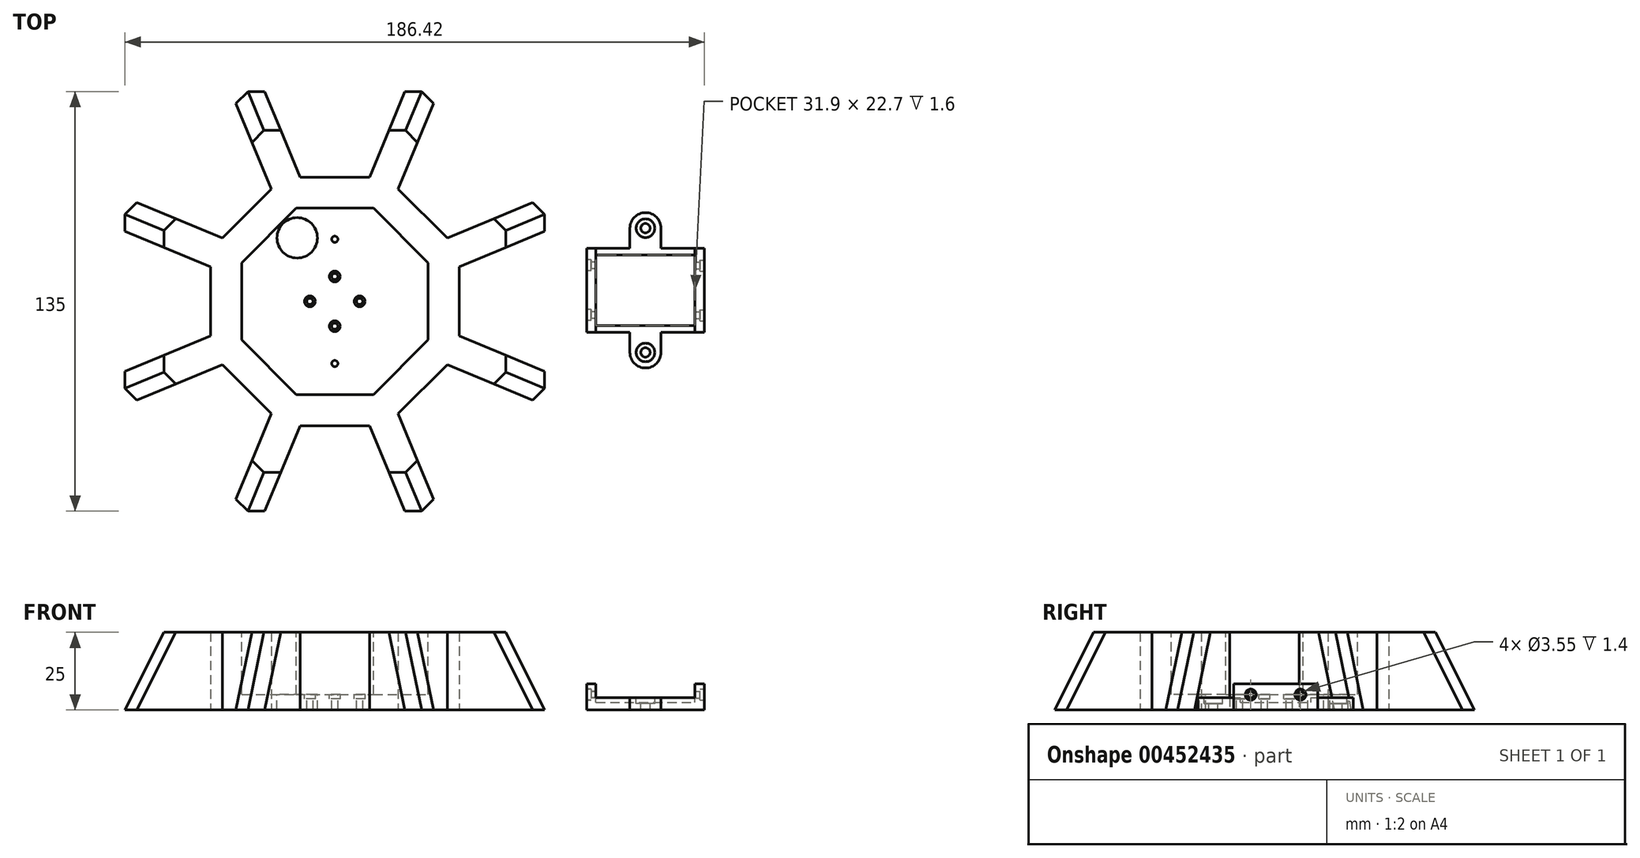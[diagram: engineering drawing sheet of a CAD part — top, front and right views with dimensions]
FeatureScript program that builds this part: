
annotation { "Feature Type Name" : "Feature", "Feature Type Description" : "" }
export const myFeature = defineFeature(function(context is Context, id is Id, definition is map)
    precondition{}
    {
        {
            var Q0;
            Q0=qCreatedBy(makeId("Top.planeOp"),FACE);
            cPlane(context, id + "F0", {"entities" : qUnion([Q0]), "cplaneType" : CPlaneType.OFFSET, "offset" : 0 * mm, "width" : 150 * mm, "height" : 150 * mm});
        }
        {
            var Q0;
            Q0=qCreatedBy(id+"F0.planeOp",FACE);
            var sketch = newSketch(context, id + "F1", { "sketchPlane" : qUnion([Q0])});
            skCircle(sketch, "E0.cCircle", {"center": v(0, 0) * mm, "radius": 75 * mm, "construction": true});
            skLineSegment(sketch, "E0.0", {"start": v(75, 31.07) * mm, "end": v(75, -31.07) * mm});
            skLineSegment(sketch, "E0.1", {"start": v(75, -31.07) * mm, "end": v(31.07, -75) * mm});
            skLineSegment(sketch, "E0.2", {"start": v(31.07, -75) * mm, "end": v(-31.07, -75) * mm});
            skLineSegment(sketch, "E0.3", {"start": v(-31.07, -75) * mm, "end": v(-75, -31.07) * mm});
            skLineSegment(sketch, "E0.4", {"start": v(-75, -31.07) * mm, "end": v(-75, 31.07) * mm});
            skLineSegment(sketch, "E0.5", {"start": v(-75, 31.07) * mm, "end": v(-31.07, 75) * mm});
            skLineSegment(sketch, "E0.6", {"start": v(-31.07, 75) * mm, "end": v(31.07, 75) * mm});
            skLineSegment(sketch, "E0.7", {"start": v(31.07, 75) * mm, "end": v(75, 31.07) * mm});
            skSolve(sketch);
        }
        {
            var Q0;
            Q0=qSketchRegion(id+"F1",true);
            extrude(context, id + "F2", {"entities" : qUnion([Q0]), "depth" : 25 * mm});
        }
        {
            var Q0;
            Q0=makeQuery(id+"F2.opExtrude","CAP_EDGE",EDGE,{"disambiguationData":[OSD([sQuery(id+"F1.wireOp",EDGE,"E0.4")])],"isStart":false});
            var Q1;
            Q1=makeQuery(id+"F2.opExtrude","CAP_EDGE",EDGE,{"disambiguationData":[OSD([sQuery(id+"F1.wireOp",EDGE,"E0.0")])],"isStart":false});
            var Q2;
            Q2=makeQuery(id+"F2.opExtrude","CAP_EDGE",EDGE,{"disambiguationData":[OSD([sQuery(id+"F1.wireOp",EDGE,"E0.7")])],"isStart":false});
            var Q3;
            Q3=makeQuery(id+"F2.opExtrude","CAP_EDGE",EDGE,{"disambiguationData":[OSD([sQuery(id+"F1.wireOp",EDGE,"E0.6")])],"isStart":false});
            var Q4;
            Q4=makeQuery(id+"F2.opExtrude","CAP_EDGE",EDGE,{"disambiguationData":[OSD([sQuery(id+"F1.wireOp",EDGE,"E0.5")])],"isStart":false});
            var Q5;
            Q5=makeQuery(id+"F2.opExtrude","CAP_EDGE",EDGE,{"disambiguationData":[OSD([sQuery(id+"F1.wireOp",EDGE,"E0.3")])],"isStart":false});
            var Q6;
            Q6=makeQuery(id+"F2.opExtrude","CAP_EDGE",EDGE,{"disambiguationData":[OSD([sQuery(id+"F1.wireOp",EDGE,"E0.2")])],"isStart":false});
            var Q7;
            Q7=makeQuery(id+"F2.opExtrude","CAP_EDGE",EDGE,{"disambiguationData":[OSD([sQuery(id+"F1.wireOp",EDGE,"E0.1")])],"isStart":false});
            chamfer(context, id + "F3", {"entities" : qUnion([Q0, Q1, Q2, Q3, Q4, Q5, Q6, Q7]), "chamferType" : ChamferType.TWO_OFFSETS, "width1" : 20 * mm, "oppositeDirection" : false, "width2" : 40 * mm, "tangentPropagation" : true});
        }
        {
            var Q0;
            Q0=makeQuery(id+"F2.opExtrude","CAP_FACE",FACE,{"disambiguationData":[OSD([sQuery(id+"F1.wireOp",EDGE,"E0.0"),sQuery(id+"F1.wireOp",EDGE,"E0.1"),sQuery(id+"F1.wireOp",EDGE,"E0.2"),sQuery(id+"F1.wireOp",EDGE,"E0.3"),sQuery(id+"F1.wireOp",EDGE,"E0.4"),sQuery(id+"F1.wireOp",EDGE,"E0.5"),sQuery(id+"F1.wireOp",EDGE,"E0.6"),sQuery(id+"F1.wireOp",EDGE,"E0.7")])],"isStart":false});
            var sketch = newSketch(context, id + "F4", { "sketchPlane" : qUnion([Q0])});
            skPoint(sketch, "E1.middle", {"position": v(0, 0) * mm});
            skLineSegment(sketch, "E2.0", {"start": v(-14.5, 35) * mm, "end": v(-35, 14.5) * mm});
            skLineSegment(sketch, "E2.1", {"start": v(14.5, 35) * mm, "end": v(-14.5, 35) * mm});
            skLineSegment(sketch, "E2.2", {"start": v(35, 14.5) * mm, "end": v(14.5, 35) * mm});
            skLineSegment(sketch, "E2.3", {"start": v(35, -14.5) * mm, "end": v(35, 14.5) * mm});
            skLineSegment(sketch, "E2.4", {"start": v(14.5, -35) * mm, "end": v(35, -14.5) * mm});
            skLineSegment(sketch, "E2.5", {"start": v(-14.5, -35) * mm, "end": v(14.5, -35) * mm});
            skLineSegment(sketch, "E2.6", {"start": v(-35, -14.5) * mm, "end": v(-14.5, -35) * mm});
            skLineSegment(sketch, "E2.7", {"start": v(-35, 14.5) * mm, "end": v(-35, -14.5) * mm});
            skLineSegment(sketch, "E3.0", {"start": v(-12.43, -30) * mm, "end": v(12.43, -30) * mm});
            skLineSegment(sketch, "E3.1", {"start": v(-30, -12.43) * mm, "end": v(-12.43, -30) * mm});
            skLineSegment(sketch, "E3.2", {"start": v(12.43, -30) * mm, "end": v(30, -12.43) * mm});
            skLineSegment(sketch, "E3.3", {"start": v(-30, 12.43) * mm, "end": v(-30, -12.43) * mm});
            skLineSegment(sketch, "E3.4", {"start": v(30, -12.43) * mm, "end": v(30, 12.43) * mm});
            skLineSegment(sketch, "E3.5", {"start": v(30, 12.43) * mm, "end": v(12.43, 30) * mm});
            skLineSegment(sketch, "E3.6", {"start": v(12.43, 30) * mm, "end": v(-12.43, 30) * mm});
            skLineSegment(sketch, "E3.7", {"start": v(-12.43, 30) * mm, "end": v(-30, 12.43) * mm});
            skSolve(sketch);
        }
        {
            var Q0;
            Q0=makeQuery(id+"F4.imprint","IMPRINT",FACE,{"disambiguationData":[TD([[makeQuery(id+"F4.imprint","IMPRINT",EDGE,{"derivedFrom":sQuery(id+"F4.wireOp",EDGE,"E1.bottom")}),-1.0]])]});
            var Q1;
            Q1=makeQuery(id+"F4.imprint","IMPRINT",FACE,{"disambiguationData":[TD([[makeQuery(id+"F4.imprint","IMPRINT",EDGE,{"derivedFrom":sQuery(id+"F4.wireOp",EDGE,"E3.0")}),1.0]])]});
            extrude(context, id + "F5", {"entities" : qUnion([Q0, Q1]), "operationType" : NewBodyOperationType.REMOVE, "oppositeDirection" : true, "depth" : 20 * mm, "offsetDistance" : 25 * mm});
        }
        {
            var Q0;
            Q0=makeQuery(id+"F5.boolean.opBoolean","COPY",FACE,{"derivedFrom":makeQuery(id+"F5.opExtrude","CAP_FACE",FACE,{"disambiguationData":[OSD([sQuery(id+"F4.wireOp",EDGE,"E3.0"),sQuery(id+"F4.wireOp",EDGE,"E3.1"),sQuery(id+"F4.wireOp",EDGE,"E3.2"),sQuery(id+"F4.wireOp",EDGE,"E3.3"),sQuery(id+"F4.wireOp",EDGE,"E3.4"),sQuery(id+"F4.wireOp",EDGE,"E3.5"),sQuery(id+"F4.wireOp",EDGE,"E3.6"),sQuery(id+"F4.wireOp",EDGE,"E3.7")])],"isStart":false})});
            var sketch = newSketch(context, id + "F6", { "sketchPlane" : qUnion([Q0])});
            skCircle(sketch, "E4", {"center": v(0, 0) * mm, "radius": 8 * mm, "construction": true});
            skCircle(sketch, "E5", {"center": v(0, 8) * mm, "radius": 1 * mm});
            skCircle(sketch, "E6", {"center": v(8, 0) * mm, "radius": 1 * mm});
            skCircle(sketch, "E7", {"center": v(0, -8) * mm, "radius": 1 * mm});
            skCircle(sketch, "E8", {"center": v(-8, 0) * mm, "radius": 1 * mm});
            skCircle(sketch, "E9", {"center": v(0, 0) * mm, "radius": 12 * mm});
            skCircle(sketch, "E10", {"center": v(0, 8) * mm, "radius": 1.75 * mm});
            skCircle(sketch, "E11", {"center": v(8, 0) * mm, "radius": 1.75 * mm});
            skCircle(sketch, "E12", {"center": v(0, -8) * mm, "radius": 1.75 * mm});
            skCircle(sketch, "E13", {"center": v(-8, 0) * mm, "radius": 1.75 * mm});
            skSolve(sketch);
        }
        {
            var Q0;
            Q0=makeQuery(id+"F6.imprint","IMPRINT",FACE,{"disambiguationData":[TD([[makeQuery(id+"F6.imprint","IMPRINT",EDGE,{"derivedFrom":sQuery(id+"F6.wireOp",EDGE,"E6")}),1.0]])]});
            var Q1;
            Q1=makeQuery(id+"F6.imprint","IMPRINT",FACE,{"disambiguationData":[TD([[makeQuery(id+"F6.imprint","IMPRINT",EDGE,{"derivedFrom":sQuery(id+"F6.wireOp",EDGE,"E5")}),1.0]])]});
            var Q2;
            Q2=makeQuery(id+"F6.imprint","IMPRINT",FACE,{"disambiguationData":[TD([[makeQuery(id+"F6.imprint","IMPRINT",EDGE,{"derivedFrom":sQuery(id+"F6.wireOp",EDGE,"E8")}),1.0]])]});
            var Q3;
            Q3=makeQuery(id+"F6.imprint","IMPRINT",FACE,{"disambiguationData":[TD([[makeQuery(id+"F6.imprint","IMPRINT",EDGE,{"derivedFrom":sQuery(id+"F6.wireOp",EDGE,"E7")}),1.0]])]});
            extrude(context, id + "F7", {"entities" : qUnion([Q0, Q1, Q2, Q3]), "operationType" : NewBodyOperationType.REMOVE, "oppositeDirection" : true, "depth" : 25 * mm, "offsetDistance" : 25 * mm});
        }
        {
            var Q0;
            Q0=makeQuery(id+"F2.opExtrude","CAP_FACE",FACE,{"disambiguationData":[OSD([sQuery(id+"F1.wireOp",EDGE,"E0.0"),sQuery(id+"F1.wireOp",EDGE,"E0.1"),sQuery(id+"F1.wireOp",EDGE,"E0.2"),sQuery(id+"F1.wireOp",EDGE,"E0.3"),sQuery(id+"F1.wireOp",EDGE,"E0.4"),sQuery(id+"F1.wireOp",EDGE,"E0.5"),sQuery(id+"F1.wireOp",EDGE,"E0.6"),sQuery(id+"F1.wireOp",EDGE,"E0.7")])],"isStart":true});
            var sketch = newSketch(context, id + "F8", { "sketchPlane" : qUnion([Q0])});
            skLineSegment(sketch, "E14.0", {"start": v(35, -14.5) * mm, "end": v(14.5, -35) * mm});
            skLineSegment(sketch, "E14.1", {"start": v(31.07, -75) * mm, "end": v(14.5, -35) * mm});
            skLineSegment(sketch, "E14.2", {"start": v(31.07, -75) * mm, "end": v(75, -31.07) * mm});
            skLineSegment(sketch, "E14.3", {"start": v(75, -31.07) * mm, "end": v(35, -14.5) * mm});
            skLineSegment(sketch, "E14.4", {"start": v(75, -31.07) * mm, "end": v(75, 31.07) * mm});
            skLineSegment(sketch, "E14.5", {"start": v(75, 31.07) * mm, "end": v(31.07, 75) * mm});
            skLineSegment(sketch, "E14.6", {"start": v(31.07, 75) * mm, "end": v(-31.07, 75) * mm});
            skLineSegment(sketch, "E14.7", {"start": v(-31.07, 75) * mm, "end": v(-75, 31.07) * mm});
            skLineSegment(sketch, "E14.8", {"start": v(-75, 31.07) * mm, "end": v(-75, -31.07) * mm});
            skLineSegment(sketch, "E14.9", {"start": v(-75, -31.07) * mm, "end": v(-31.07, -75) * mm});
            skLineSegment(sketch, "E14.10", {"start": v(-31.07, -75) * mm, "end": v(31.07, -75) * mm});
            skLineSegment(sketch, "E14.11", {"start": v(-31.07, -75) * mm, "end": v(-14.5, -35) * mm});
            skLineSegment(sketch, "E14.12", {"start": v(-35, -14.5) * mm, "end": v(-75, -31.07) * mm});
            skLineSegment(sketch, "E14.13", {"start": v(-35, 14.5) * mm, "end": v(-75, 31.07) * mm});
            skLineSegment(sketch, "E14.14", {"start": v(-14.5, 35) * mm, "end": v(-31.07, 75) * mm});
            skLineSegment(sketch, "E14.15", {"start": v(14.5, 35) * mm, "end": v(31.07, 75) * mm});
            skLineSegment(sketch, "E14.16", {"start": v(75, 31.07) * mm, "end": v(35, 14.5) * mm});
            skLineSegment(sketch, "E14.17", {"start": v(35, 14.5) * mm, "end": v(35, -14.5) * mm});
            skLineSegment(sketch, "E14.18", {"start": v(14.5, 35) * mm, "end": v(35, 14.5) * mm});
            skLineSegment(sketch, "E14.19", {"start": v(-14.5, 35) * mm, "end": v(14.5, 35) * mm});
            skLineSegment(sketch, "E14.20", {"start": v(-35, 14.5) * mm, "end": v(-14.5, 35) * mm});
            skLineSegment(sketch, "E14.21", {"start": v(-35, -14.5) * mm, "end": v(-35, 14.5) * mm});
            skLineSegment(sketch, "E14.22", {"start": v(-14.5, -35) * mm, "end": v(-35, -14.5) * mm});
            skLineSegment(sketch, "E14.23", {"start": v(14.5, -35) * mm, "end": v(-14.5, -35) * mm});
            skLineSegment(sketch, "E15.0", {"start": v(11.16, 40) * mm, "end": v(23.58, 70) * mm});
            skLineSegment(sketch, "E15.1", {"start": v(-11.16, 40) * mm, "end": v(11.16, 40) * mm});
            skLineSegment(sketch, "E15.2", {"start": v(-11.16, 40) * mm, "end": v(-23.58, 70) * mm});
            skLineSegment(sketch, "E15.3", {"start": v(23.58, 70) * mm, "end": v(-23.58, 70) * mm});
            skLineSegment(sketch, "E16.0", {"start": v(20.4, 36.17) * mm, "end": v(32.82, 66.17) * mm});
            skLineSegment(sketch, "E16.1", {"start": v(20.4, 36.17) * mm, "end": v(36.17, 20.4) * mm});
            skLineSegment(sketch, "E16.2", {"start": v(66.17, 32.82) * mm, "end": v(36.17, 20.4) * mm});
            skLineSegment(sketch, "E16.3", {"start": v(66.17, 32.82) * mm, "end": v(32.82, 66.17) * mm});
            skLineSegment(sketch, "E17.0", {"start": v(70, 23.58) * mm, "end": v(40, 11.16) * mm});
            skLineSegment(sketch, "E17.1", {"start": v(70, -23.58) * mm, "end": v(70, 23.58) * mm});
            skLineSegment(sketch, "E17.2", {"start": v(70, -23.58) * mm, "end": v(40, -11.16) * mm});
            skLineSegment(sketch, "E17.3", {"start": v(40, 11.16) * mm, "end": v(40, -11.16) * mm});
            skLineSegment(sketch, "E18.0", {"start": v(66.17, -32.82) * mm, "end": v(36.17, -20.4) * mm});
            skLineSegment(sketch, "E18.1", {"start": v(32.82, -66.17) * mm, "end": v(66.17, -32.82) * mm});
            skLineSegment(sketch, "E18.2", {"start": v(32.82, -66.17) * mm, "end": v(20.4, -36.17) * mm});
            skLineSegment(sketch, "E18.3", {"start": v(36.17, -20.4) * mm, "end": v(20.4, -36.17) * mm});
            skLineSegment(sketch, "E19.0", {"start": v(23.58, -70) * mm, "end": v(11.16, -40) * mm});
            skLineSegment(sketch, "E19.1", {"start": v(-23.58, -70) * mm, "end": v(23.58, -70) * mm});
            skLineSegment(sketch, "E19.2", {"start": v(-23.58, -70) * mm, "end": v(-11.16, -40) * mm});
            skLineSegment(sketch, "E19.3", {"start": v(11.16, -40) * mm, "end": v(-11.16, -40) * mm});
            skLineSegment(sketch, "E20.0", {"start": v(-32.82, -66.17) * mm, "end": v(-20.4, -36.17) * mm});
            skLineSegment(sketch, "E20.1", {"start": v(-66.17, -32.82) * mm, "end": v(-32.82, -66.17) * mm});
            skLineSegment(sketch, "E20.2", {"start": v(-36.17, -20.4) * mm, "end": v(-66.17, -32.82) * mm});
            skLineSegment(sketch, "E20.3", {"start": v(-20.4, -36.17) * mm, "end": v(-36.17, -20.4) * mm});
            skLineSegment(sketch, "E21.0", {"start": v(-40, -11.16) * mm, "end": v(-40, 11.16) * mm});
            skLineSegment(sketch, "E21.1", {"start": v(-40, -11.16) * mm, "end": v(-70, -23.58) * mm});
            skLineSegment(sketch, "E21.2", {"start": v(-70, 23.58) * mm, "end": v(-70, -23.58) * mm});
            skLineSegment(sketch, "E21.3", {"start": v(-40, 11.16) * mm, "end": v(-70, 23.58) * mm});
            skLineSegment(sketch, "E22.0", {"start": v(-36.17, 20.4) * mm, "end": v(-20.4, 36.17) * mm});
            skLineSegment(sketch, "E22.1", {"start": v(-36.17, 20.4) * mm, "end": v(-66.17, 32.82) * mm});
            skLineSegment(sketch, "E22.2", {"start": v(-32.82, 66.17) * mm, "end": v(-66.17, 32.82) * mm});
            skLineSegment(sketch, "E22.3", {"start": v(-20.4, 36.17) * mm, "end": v(-32.82, 66.17) * mm});
            skSolve(sketch);
        }
        {
            var Q0;
            Q0=makeQuery(id+"F8.imprint","IMPRINT",FACE,{"disambiguationData":[TD([[makeQuery(id+"F8.imprint","IMPRINT",EDGE,{"derivedFrom":sQuery(id+"F8.wireOp",EDGE,"E22.0")}),1.0]])]});
            var Q1;
            Q1=makeQuery(id+"F8.imprint","IMPRINT",FACE,{"disambiguationData":[TD([[makeQuery(id+"F8.imprint","IMPRINT",EDGE,{"derivedFrom":sQuery(id+"F8.wireOp",EDGE,"E15.0")}),1.0]])]});
            var Q2;
            Q2=makeQuery(id+"F8.imprint","IMPRINT",FACE,{"disambiguationData":[TD([[makeQuery(id+"F8.imprint","IMPRINT",EDGE,{"derivedFrom":sQuery(id+"F8.wireOp",EDGE,"E16.0")}),-1.0]])]});
            var Q3;
            Q3=makeQuery(id+"F8.imprint","IMPRINT",FACE,{"disambiguationData":[TD([[makeQuery(id+"F8.imprint","IMPRINT",EDGE,{"derivedFrom":sQuery(id+"F8.wireOp",EDGE,"E17.0")}),1.0]])]});
            var Q4;
            Q4=makeQuery(id+"F8.imprint","IMPRINT",FACE,{"disambiguationData":[TD([[makeQuery(id+"F8.imprint","IMPRINT",EDGE,{"derivedFrom":sQuery(id+"F8.wireOp",EDGE,"E18.0")}),1.0]])]});
            var Q5;
            Q5=makeQuery(id+"F8.imprint","IMPRINT",FACE,{"disambiguationData":[TD([[makeQuery(id+"F8.imprint","IMPRINT",EDGE,{"derivedFrom":sQuery(id+"F8.wireOp",EDGE,"E19.0")}),1.0]])]});
            var Q6;
            Q6=makeQuery(id+"F8.imprint","IMPRINT",FACE,{"disambiguationData":[TD([[makeQuery(id+"F8.imprint","IMPRINT",EDGE,{"derivedFrom":sQuery(id+"F8.wireOp",EDGE,"E20.0")}),1.0]])]});
            var Q7;
            Q7=makeQuery(id+"F8.imprint","IMPRINT",FACE,{"disambiguationData":[TD([[makeQuery(id+"F8.imprint","IMPRINT",EDGE,{"derivedFrom":sQuery(id+"F8.wireOp",EDGE,"E21.0")}),1.0]])]});
            extrude(context, id + "F9", {"entities" : qUnion([Q0, Q1, Q2, Q3, Q4, Q5, Q6, Q7]), "operationType" : NewBodyOperationType.REMOVE, "oppositeDirection" : true, "depth" : 25 * mm});
        }
        {
            var Q0;
            Q0=makeQuery(id+"F6.imprint","IMPRINT",FACE,{"disambiguationData":[TD([[makeQuery(id+"F6.imprint","IMPRINT",EDGE,{"derivedFrom":sQuery(id+"F6.wireOp",EDGE,"E8")}),-1.0]])]});
            var Q1;
            Q1=makeQuery(id+"F6.imprint","IMPRINT",FACE,{"disambiguationData":[TD([[makeQuery(id+"F6.imprint","IMPRINT",EDGE,{"derivedFrom":sQuery(id+"F6.wireOp",EDGE,"E5")}),-1.0]])]});
            var Q2;
            Q2=makeQuery(id+"F6.imprint","IMPRINT",FACE,{"disambiguationData":[TD([[makeQuery(id+"F6.imprint","IMPRINT",EDGE,{"derivedFrom":sQuery(id+"F6.wireOp",EDGE,"E6")}),-1.0]])]});
            var Q3;
            Q3=makeQuery(id+"F6.imprint","IMPRINT",FACE,{"disambiguationData":[TD([[makeQuery(id+"F6.imprint","IMPRINT",EDGE,{"derivedFrom":sQuery(id+"F6.wireOp",EDGE,"E7")}),-1.0]])]});
            extrude(context, id + "F10", {"entities" : qUnion([Q0, Q1, Q2, Q3]), "operationType" : NewBodyOperationType.REMOVE, "oppositeDirection" : true, "depth" : 1.4 * mm, "offsetDistance" : 25 * mm});
        }
        {
            var Q0;
            Q0=qCreatedBy(id+"F0.planeOp",FACE);
            var sketch = newSketch(context, id + "F11", { "sketchPlane" : qUnion([Q0])});
            skLineSegment(sketch, "E23", {"start": v(81.02, 17.06) * mm, "end": v(118.92, 17.06) * mm});
            skLineSegment(sketch, "E24", {"start": v(118.92, 17.06) * mm, "end": v(118.92, -9.94) * mm});
            skLineSegment(sketch, "E25", {"start": v(118.92, -9.94) * mm, "end": v(81.02, -9.94) * mm});
            skLineSegment(sketch, "E26", {"start": v(81.02, -9.94) * mm, "end": v(81.02, 17.06) * mm});
            skLineSegment(sketch, "E27", {"start": v(84.02, 17.06) * mm, "end": v(84.02, -9.94) * mm});
            skLineSegment(sketch, "E28", {"start": v(115.92, 17.06) * mm, "end": v(115.92, -9.94) * mm});
            skPoint(sketch, "E29", {"position": v(99.97, 17.06) * mm});
            skArc(sketch, "E30", {"start": v(104.97, 23.56) * mm, "mid": v(99.97, 28.56) * mm, "end": v(94.97, 23.56) * mm});
            skPoint(sketch, "E31", {"position": v(94.97, 17.06) * mm});
            skPoint(sketch, "E32", {"position": v(104.97, 17.06) * mm});
            skLineSegment(sketch, "E33", {"start": v(94.97, 17.06) * mm, "end": v(94.97, 23.56) * mm});
            skLineSegment(sketch, "E34", {"start": v(104.97, 17.06) * mm, "end": v(104.97, 23.56) * mm});
            skPoint(sketch, "E35", {"position": v(99.97, -9.94) * mm});
            skPoint(sketch, "E36", {"position": v(104.97, -9.94) * mm});
            skPoint(sketch, "E37", {"position": v(94.97, -9.94) * mm});
            skArc(sketch, "E38", {"start": v(94.97, -16.44) * mm, "mid": v(99.97, -21.44) * mm, "end": v(104.97, -16.44) * mm});
            skLineSegment(sketch, "E39", {"start": v(94.97, -9.94) * mm, "end": v(94.97, -16.44) * mm});
            skLineSegment(sketch, "E40", {"start": v(104.97, -9.94) * mm, "end": v(104.97, -16.44) * mm});
            skSolve(sketch);
        }
        {
            var Q0;
            Q0 = qSketchRegion(id + "F11", true);
            extrude(context, id + "F12", {"entities" : qUnion([Q0]), "depth" : 4 * mm, "offsetDistance" : 25 * mm});
        }
        {
            var Q0;
            {var subQ0=sQuery(id+"F11.wireOp",EDGE,"E26");Q0=makeQuery(id+"F11.imprint","IMPRINT",FACE,{"disambiguationData":[TD([[makeQuery(id+"F11.imprint","IMPRINT",EDGE,{"derivedFrom":subQ0}),-1.0]])]});}
            var Q1;
            {var subQ0=sQuery(id+"F11.wireOp",EDGE,"E24");Q1=makeQuery(id+"F11.imprint","IMPRINT",FACE,{"disambiguationData":[TD([[makeQuery(id+"F11.imprint","IMPRINT",EDGE,{"derivedFrom":subQ0}),-1.0]])]});}
            extrude(context, id + "F13", {"entities" : qUnion([Q0, Q1]), "operationType" : NewBodyOperationType.ADD, "depth" : 8.4 * mm, "offsetDistance" : 25 * mm});
        }
        {
            var Q0;
            Q0=makeQuery(id+"F12.opExtrude","CAP_FACE",FACE,{"disambiguationData":[OSD([sQuery(id+"F11.wireOp",EDGE,"E23"),sQuery(id+"F11.wireOp",EDGE,"E24"),sQuery(id+"F11.wireOp",EDGE,"E25"),sQuery(id+"F11.wireOp",EDGE,"E26"),sQuery(id+"F11.wireOp",EDGE,"E30"),sQuery(id+"F11.wireOp",EDGE,"E33"),sQuery(id+"F11.wireOp",EDGE,"E34"),sQuery(id+"F11.wireOp",EDGE,"E38"),sQuery(id+"F11.wireOp",EDGE,"E39"),sQuery(id+"F11.wireOp",EDGE,"E40")])],"isStart":false});
            var sketch = newSketch(context, id + "F14", { "sketchPlane" : qUnion([Q0])});
            skLineSegment(sketch, "E41.0", {"start": v(81.02, 17.06) * mm, "end": v(118.92, 17.06) * mm});
            skLineSegment(sketch, "E41.1", {"start": v(118.92, -9.94) * mm, "end": v(81.02, -9.94) * mm});
            skLineSegment(sketch, "E42.0", {"start": v(115.92, 17.06) * mm, "end": v(115.92, -9.94) * mm});
            skLineSegment(sketch, "E42.1", {"start": v(84.02, 17.06) * mm, "end": v(84.02, -9.94) * mm});
            skPoint(sketch, "E43", {"position": v(84.02, 3.56) * mm});
            skPoint(sketch, "E44", {"position": v(115.92, 3.56) * mm});
            skLineSegment(sketch, "E45", {"start": v(84.02, 14.91) * mm, "end": v(115.92, 14.91) * mm});
            skLineSegment(sketch, "E46", {"start": v(115.92, -7.79) * mm, "end": v(84.02, -7.79) * mm});
            skSolve(sketch);
        }
        {
            var Q0;
            {var subQ0=sQuery(id+"F14.wireOp",EDGE,"E45");Q0=makeQuery(id+"F14.imprint","IMPRINT",FACE,{"disambiguationData":[TD([[makeQuery(id+"F14.imprint","IMPRINT",EDGE,{"derivedFrom":subQ0}),-1.0]])]});}
            extrude(context, id + "F15", {"entities" : qUnion([Q0]), "operationType" : NewBodyOperationType.REMOVE, "oppositeDirection" : true, "depth" : 1.6 * mm, "offsetDistance" : 25 * mm});
        }
        {
            var Q0;
            {var subQ0=sQuery(id+"F11.wireOp",EDGE,"E24");Q0=makeQuery(id+"F13.boolean.opBoolean","MERGE",FACE,{"derivedFrom":[makeQuery(id+"F12.opExtrude","SWEPT_FACE",FACE,{"disambiguationData":[OSD([subQ0])]}),makeQuery(id+"F13.opExtrude","SWEPT_FACE",FACE,{"disambiguationData":[OSD([subQ0])]})]});}
            var sketch = newSketch(context, id + "F16", { "sketchPlane" : qUnion([Q0])});
            skLineSegment(sketch, "E47.0", {"start": v(-7.79, 2.4) * mm, "end": v(14.91, 2.4) * mm});
            skLineSegment(sketch, "E48", {"start": v(3.56, 2.4) * mm, "end": v(3.56, 4.9) * mm, "construction": true});
            skLineSegment(sketch, "E49", {"start": v(3.56, 4.9) * mm, "end": v(-4.44, 4.9) * mm, "construction": true});
            skLineSegment(sketch, "E50", {"start": v(3.56, 4.9) * mm, "end": v(11.56, 4.9) * mm, "construction": true});
            skCircle(sketch, "E51", {"center": v(11.56, 4.9) * mm, "radius": 1.77 * mm});
            skCircle(sketch, "E52", {"center": v(-4.44, 4.9) * mm, "radius": 1.77 * mm});
            skCircle(sketch, "E53", {"center": v(-4.44, 4.9) * mm, "radius": 1.05 * mm});
            skCircle(sketch, "E54", {"center": v(11.56, 4.9) * mm, "radius": 1.05 * mm});
            skSolve(sketch);
        }
        {
            var Q0;
            Q0=makeQuery(id+"F16.imprint","IMPRINT",FACE,{"disambiguationData":[TD([[makeQuery(id+"F16.imprint","IMPRINT",EDGE,{"derivedFrom":sQuery(id+"F16.wireOp",EDGE,"E54")}),1.0]])]});
            var Q1;
            Q1=makeQuery(id+"F16.imprint","IMPRINT",FACE,{"disambiguationData":[TD([[makeQuery(id+"F16.imprint","IMPRINT",EDGE,{"derivedFrom":sQuery(id+"F16.wireOp",EDGE,"E53")}),1.0]])]});
            extrude(context, id + "F17", {"entities" : qUnion([Q0, Q1]), "operationType" : NewBodyOperationType.REMOVE, "oppositeDirection" : true, "depth" : 5 * mm, "offsetDistance" : 25 * mm});
        }
        {
            var Q0;
            Q0=makeQuery(id+"F16.imprint","IMPRINT",FACE,{"disambiguationData":[TD([[makeQuery(id+"F16.imprint","IMPRINT",EDGE,{"derivedFrom":sQuery(id+"F16.wireOp",EDGE,"E52")}),1.0]])]});
            var Q1;
            Q1=makeQuery(id+"F16.imprint","IMPRINT",FACE,{"disambiguationData":[TD([[makeQuery(id+"F16.imprint","IMPRINT",EDGE,{"derivedFrom":sQuery(id+"F16.wireOp",EDGE,"E51")}),1.0]])]});
            extrude(context, id + "F18", {"entities" : qUnion([Q0, Q1]), "operationType" : NewBodyOperationType.REMOVE, "oppositeDirection" : true, "depth" : 1.4 * mm, "offsetDistance" : 25 * mm});
        }
        {
            var Q0;
            {var subQ0=sQuery(id+"F11.wireOp",EDGE,"E26");Q0=makeQuery(id+"F13.boolean.opBoolean","MERGE",FACE,{"derivedFrom":[makeQuery(id+"F12.opExtrude","SWEPT_FACE",FACE,{"disambiguationData":[OSD([subQ0])]}),makeQuery(id+"F13.opExtrude","SWEPT_FACE",FACE,{"disambiguationData":[OSD([subQ0])]})]});}
            var sketch = newSketch(context, id + "F19", { "sketchPlane" : qUnion([Q0])});
            skLineSegment(sketch, "E55.0", {"start": v(7.79, 2.4) * mm, "end": v(-14.91, 2.4) * mm});
            skLineSegment(sketch, "E56", {"start": v(-3.56, 2.4) * mm, "end": v(-3.58, 4.9) * mm, "construction": true});
            skLineSegment(sketch, "E57", {"start": v(-3.58, 4.9) * mm, "end": v(-11.58, 4.85) * mm, "construction": true});
            skLineSegment(sketch, "E58", {"start": v(-3.58, 4.9) * mm, "end": v(4.42, 4.95) * mm, "construction": true});
            skCircle(sketch, "E59", {"center": v(-11.58, 4.85) * mm, "radius": 1.77 * mm});
            skCircle(sketch, "E60", {"center": v(4.42, 4.95) * mm, "radius": 1.77 * mm});
            skCircle(sketch, "E61", {"center": v(-11.58, 4.85) * mm, "radius": 1.05 * mm});
            skCircle(sketch, "E62", {"center": v(4.42, 4.95) * mm, "radius": 1.05 * mm});
            skSolve(sketch);
        }
        {
            var Q0;
            Q0=makeQuery(id+"F19.imprint","IMPRINT",FACE,{"disambiguationData":[TD([[makeQuery(id+"F19.imprint","IMPRINT",EDGE,{"derivedFrom":sQuery(id+"F19.wireOp",EDGE,"E62")}),1.0]])]});
            var Q1;
            Q1=makeQuery(id+"F19.imprint","IMPRINT",FACE,{"disambiguationData":[TD([[makeQuery(id+"F19.imprint","IMPRINT",EDGE,{"derivedFrom":sQuery(id+"F19.wireOp",EDGE,"E61")}),1.0]])]});
            extrude(context, id + "F20", {"entities" : qUnion([Q0, Q1]), "operationType" : NewBodyOperationType.REMOVE, "oppositeDirection" : true, "depth" : 4 * mm, "offsetDistance" : 25 * mm});
        }
        {
            var Q0;
            Q0=makeQuery(id+"F19.imprint","IMPRINT",FACE,{"disambiguationData":[TD([[makeQuery(id+"F19.imprint","IMPRINT",EDGE,{"derivedFrom":sQuery(id+"F19.wireOp",EDGE,"E59")}),1.0]])]});
            var Q1;
            Q1=makeQuery(id+"F19.imprint","IMPRINT",FACE,{"disambiguationData":[TD([[makeQuery(id+"F19.imprint","IMPRINT",EDGE,{"derivedFrom":sQuery(id+"F19.wireOp",EDGE,"E60")}),1.0]])]});
            extrude(context, id + "F21", {"entities" : qUnion([Q0, Q1]), "operationType" : NewBodyOperationType.REMOVE, "oppositeDirection" : true, "depth" : 1.4 * mm, "offsetDistance" : 25 * mm});
        }
        {
            var Q0;
            {var subQ0=sQuery(id+"F11.wireOp",EDGE,"E24");var subQ1=sQuery(id+"F11.wireOp",EDGE,"E23");var subQ5=sQuery(id+"F11.wireOp",EDGE,"E26");var subQ9=sQuery(id+"F11.wireOp",EDGE,"E33");var subQ10=sQuery(id+"F11.wireOp",EDGE,"E34");var subQ11=sQuery(id+"F11.wireOp",EDGE,"E30");Q0=makeQuery(id+"F15.boolean.opBoolean","SPLIT",FACE,{"disambiguationData":[TD([makeQuery(id+"F12.opExtrude","SWEPT_FACE",FACE,{"disambiguationData":[OSD([subQ11])]})])],"derivedFrom":makeQuery(id+"F12.opExtrude","CAP_FACE",FACE,{"disambiguationData":[OSD([subQ1,subQ0,sQuery(id+"F11.wireOp",EDGE,"E25"),subQ5,subQ11,subQ9,subQ10,sQuery(id+"F11.wireOp",EDGE,"E38"),sQuery(id+"F11.wireOp",EDGE,"E39"),sQuery(id+"F11.wireOp",EDGE,"E40")])],"isStart":false})});}
            var sketch = newSketch(context, id + "F22", { "sketchPlane" : qUnion([Q0])});
            skPoint(sketch, "E63.0", {"position": v(99.97, 23.56) * mm});
            skPoint(sketch, "E63.1", {"position": v(99.97, -16.44) * mm});
            skCircle(sketch, "E64", {"center": v(99.97, -16.44) * mm, "radius": 3 * mm});
            skCircle(sketch, "E65", {"center": v(99.97, 23.56) * mm, "radius": 3 * mm});
            skCircle(sketch, "E66", {"center": v(99.97, 23.56) * mm, "radius": 1.5 * mm});
            skCircle(sketch, "E67", {"center": v(99.97, -16.44) * mm, "radius": 1.5 * mm});
            skSolve(sketch);
        }
        {
            var Q0;
            Q0=makeQuery(id+"F22.imprint","IMPRINT",FACE,{"disambiguationData":[TD([[makeQuery(id+"F22.imprint","IMPRINT",EDGE,{"derivedFrom":sQuery(id+"F22.wireOp",EDGE,"E66")}),1.0]])]});
            var Q1;
            Q1=makeQuery(id+"F22.imprint","IMPRINT",FACE,{"disambiguationData":[TD([[makeQuery(id+"F22.imprint","IMPRINT",EDGE,{"derivedFrom":sQuery(id+"F22.wireOp",EDGE,"E67")}),1.0]])]});
            extrude(context, id + "F23", {"entities" : qUnion([Q0, Q1]), "operationType" : NewBodyOperationType.REMOVE, "oppositeDirection" : true, "depth" : 25 * mm, "offsetDistance" : 25 * mm});
        }
        {
            var Q0;
            Q0=makeQuery(id+"F22.imprint","IMPRINT",FACE,{"disambiguationData":[TD([[makeQuery(id+"F22.imprint","IMPRINT",EDGE,{"derivedFrom":sQuery(id+"F22.wireOp",EDGE,"E64")}),1.0]])]});
            var Q1;
            Q1=makeQuery(id+"F22.imprint","IMPRINT",FACE,{"disambiguationData":[TD([[makeQuery(id+"F22.imprint","IMPRINT",EDGE,{"derivedFrom":sQuery(id+"F22.wireOp",EDGE,"E65")}),1.0]])]});
            extrude(context, id + "F24", {"entities" : qUnion([Q0, Q1]), "operationType" : NewBodyOperationType.REMOVE, "oppositeDirection" : true, "depth" : 2 * mm, "offsetDistance" : 25 * mm});
        }
        {
            var Q0;
            Q0=makeQuery(id+"F5.boolean.opBoolean","COPY",FACE,{"derivedFrom":makeQuery(id+"F5.opExtrude","CAP_FACE",FACE,{"disambiguationData":[OSD([sQuery(id+"F4.wireOp",EDGE,"E3.0"),sQuery(id+"F4.wireOp",EDGE,"E3.1"),sQuery(id+"F4.wireOp",EDGE,"E3.2"),sQuery(id+"F4.wireOp",EDGE,"E3.3"),sQuery(id+"F4.wireOp",EDGE,"E3.4"),sQuery(id+"F4.wireOp",EDGE,"E3.5"),sQuery(id+"F4.wireOp",EDGE,"E3.6"),sQuery(id+"F4.wireOp",EDGE,"E3.7")])],"isStart":false})});
            var sketch = newSketch(context, id + "F25", { "sketchPlane" : qUnion([Q0])});
            skLineSegment(sketch, "E68", {"start": v(0, 0) * mm, "end": v(0, 20) * mm, "construction": true});
            skLineSegment(sketch, "E69", {"start": v(0, 0) * mm, "end": v(0, -20) * mm, "construction": true});
            skCircle(sketch, "E70", {"center": v(0, -20) * mm, "radius": 1 * mm});
            skCircle(sketch, "E71", {"center": v(0, 20) * mm, "radius": 1 * mm});
            skSolve(sketch);
        }
        {
            var Q0;
            Q0=makeQuery(id+"F25.imprint","IMPRINT",FACE,{"disambiguationData":[TD([[makeQuery(id+"F25.imprint","IMPRINT",EDGE,{"derivedFrom":sQuery(id+"F25.wireOp",EDGE,"E71")}),1.0]])]});
            var Q1;
            Q1=makeQuery(id+"F25.imprint","IMPRINT",FACE,{"disambiguationData":[TD([[makeQuery(id+"F25.imprint","IMPRINT",EDGE,{"derivedFrom":sQuery(id+"F25.wireOp",EDGE,"E70")}),1.0]])]});
            extrude(context, id + "F26", {"entities" : qUnion([Q0, Q1]), "operationType" : NewBodyOperationType.REMOVE, "oppositeDirection" : true, "depth" : 25 * mm, "offsetDistance" : 25 * mm});
        }
        {
            var Q0;
            Q0=makeQuery(id+"F5.boolean.opBoolean","COPY",FACE,{"derivedFrom":makeQuery(id+"F5.opExtrude","CAP_FACE",FACE,{"disambiguationData":[OSD([sQuery(id+"F4.wireOp",EDGE,"E3.0"),sQuery(id+"F4.wireOp",EDGE,"E3.1"),sQuery(id+"F4.wireOp",EDGE,"E3.2"),sQuery(id+"F4.wireOp",EDGE,"E3.3"),sQuery(id+"F4.wireOp",EDGE,"E3.4"),sQuery(id+"F4.wireOp",EDGE,"E3.5"),sQuery(id+"F4.wireOp",EDGE,"E3.6"),sQuery(id+"F4.wireOp",EDGE,"E3.7")])],"isStart":false})});
            var sketch = newSketch(context, id + "F27", { "sketchPlane" : qUnion([Q0])});
            skLineSegment(sketch, "E72", {"start": v(-18.95, 13.5) * mm, "end": v(18.95, 13.5) * mm, "construction": true});
            skLineSegment(sketch, "E73", {"start": v(18.95, 13.5) * mm, "end": v(18.95, -13.5) * mm, "construction": true});
            skLineSegment(sketch, "E74", {"start": v(18.95, -13.5) * mm, "end": v(-18.95, -13.5) * mm, "construction": true});
            skLineSegment(sketch, "E75", {"start": v(-18.95, -13.5) * mm, "end": v(-18.95, 13.5) * mm, "construction": true});
            skLineSegment(sketch, "E76", {"start": v(-15.95, 13.5) * mm, "end": v(-15.95, -13.5) * mm, "construction": true});
            skLineSegment(sketch, "E77", {"start": v(15.95, 13.5) * mm, "end": v(15.95, -13.5) * mm, "construction": true});
            skPoint(sketch, "E78", {"position": v(0, 13.5) * mm});
            skArc(sketch, "E79", {"start": v(5, 20) * mm, "mid": v(0, 25) * mm, "end": v(-5, 20) * mm, "construction": true});
            skPoint(sketch, "E80", {"position": v(-5, 13.5) * mm});
            skPoint(sketch, "E81", {"position": v(5, 13.5) * mm});
            skLineSegment(sketch, "E82", {"start": v(-5, 13.5) * mm, "end": v(-5, 20) * mm, "construction": true});
            skLineSegment(sketch, "E83", {"start": v(5, 13.5) * mm, "end": v(5, 20) * mm, "construction": true});
            skPoint(sketch, "E84", {"position": v(0, -13.5) * mm});
            skPoint(sketch, "E85", {"position": v(5, -13.5) * mm});
            skPoint(sketch, "E86", {"position": v(-5, -13.5) * mm});
            skArc(sketch, "E87", {"start": v(-5, -20) * mm, "mid": v(0, -25) * mm, "end": v(5, -20) * mm, "construction": true});
            skLineSegment(sketch, "E88", {"start": v(-5, -13.5) * mm, "end": v(-5, -20) * mm, "construction": true});
            skLineSegment(sketch, "E89", {"start": v(5, -13.5) * mm, "end": v(5, -20) * mm, "construction": true});
            skCircle(sketch, "E90", {"center": v(-12.1, 20.44) * mm, "radius": 6.5 * mm});
            skSolve(sketch);
        }
        {
            var Q0;
            Q0=makeQuery(id+"F27.imprint","IMPRINT",FACE,{"disambiguationData":[TD([[makeQuery(id+"F27.imprint","IMPRINT",EDGE,{"derivedFrom":sQuery(id+"F27.wireOp",EDGE,"E90")}),1.0]])]});
            extrude(context, id + "F28", {"entities" : qUnion([Q0]), "operationType" : NewBodyOperationType.REMOVE, "oppositeDirection" : true, "depth" : 25 * mm, "offsetDistance" : 25 * mm});
        }
    });
